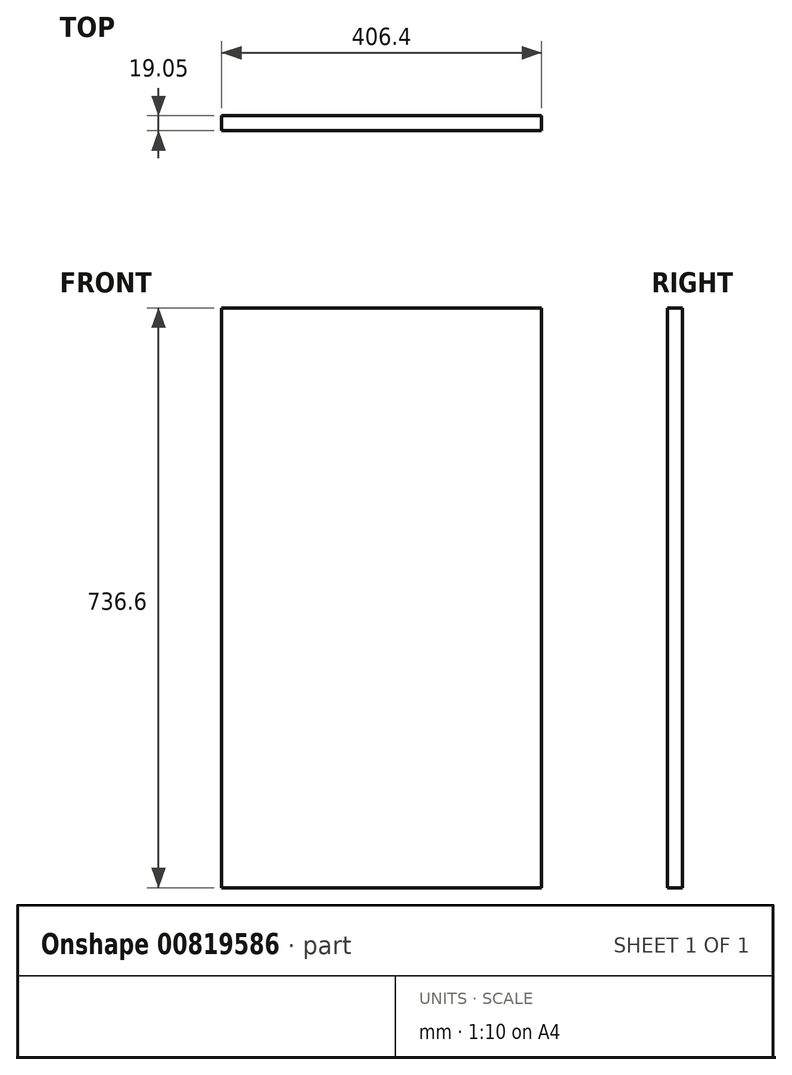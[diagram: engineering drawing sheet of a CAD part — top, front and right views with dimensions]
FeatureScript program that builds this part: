
annotation { "Feature Type Name" : "Feature", "Feature Type Description" : "" }
export const myFeature = defineFeature(function(context is Context, id is Id, definition is map)
    precondition{}
    {
        {
            var Q0;
            Q0=qCreatedBy(makeId("Front.planeOp"),FACE);
            var sketch = newSketch(context, id + "F0", { "sketchPlane" : qUnion([Q0])});
            skLineSegment(sketch, "E0.bottom", {"start": v(203.2, 368.3) * mm, "end": v(-203.2, 368.3) * mm});
            skLineSegment(sketch, "E0.top", {"start": v(203.2, -368.3) * mm, "end": v(-203.2, -368.3) * mm});
            skLineSegment(sketch, "E0.left", {"start": v(203.2, 368.3) * mm, "end": v(203.2, -368.3) * mm});
            skLineSegment(sketch, "E0.right", {"start": v(-203.2, 368.3) * mm, "end": v(-203.2, -368.3) * mm});
            skPoint(sketch, "E0.middle", {"position": v(0, 0) * mm});
            skSolve(sketch);
        }
        {
            var Q0;
            Q0=makeQuery(id+"F0.imprint","IMPRINT",FACE,{"disambiguationData":[TD([[makeQuery(id+"F0.imprint","IMPRINT",EDGE,{"derivedFrom":sQuery(id+"F0.wireOp",EDGE,"E0.bottom")}),1.0]])]});
            extrude(context, id + "F1", {"entities" : qUnion([Q0]), "depth" : 19.05 * mm, "offsetDistance" : 25.4 * mm});
        }
    });
